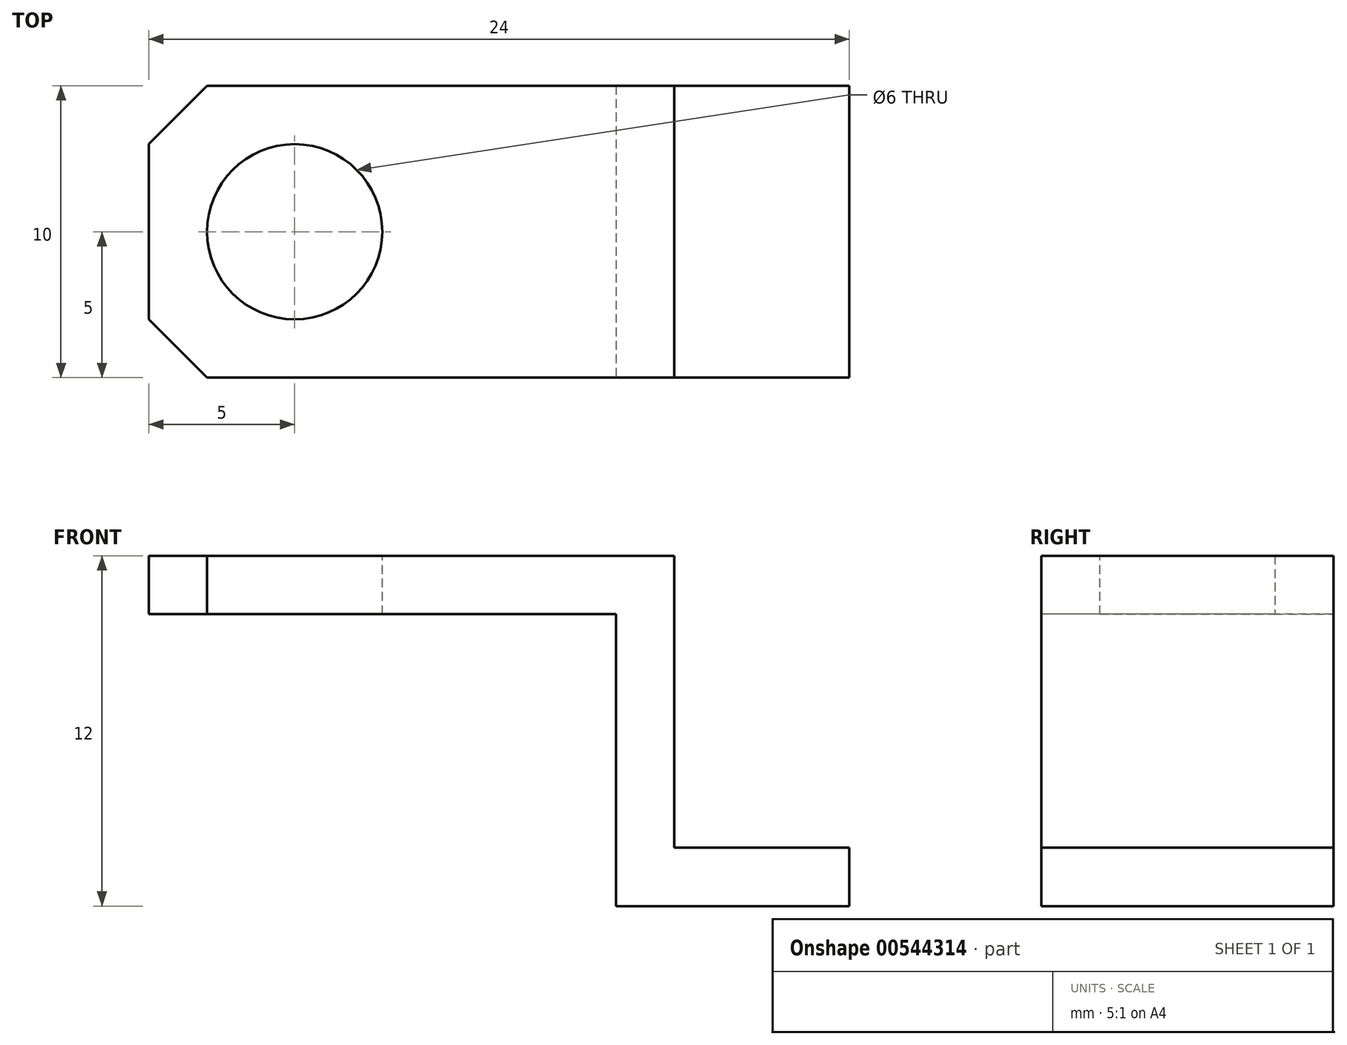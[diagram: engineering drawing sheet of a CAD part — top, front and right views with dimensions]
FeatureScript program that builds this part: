
annotation { "Feature Type Name" : "Feature", "Feature Type Description" : "" }
export const myFeature = defineFeature(function(context is Context, id is Id, definition is map)
    precondition{}
    {
        {
            var Q0;
            Q0=qCreatedBy(makeId("Top.planeOp"),FACE);
            var sketch = newSketch(context, id + "F0", { "sketchPlane" : qUnion([Q0])});
            skLineSegment(sketch, "E0.bottom", {"start": v(0, 0) * mm, "end": v(16, 0) * mm});
            skLineSegment(sketch, "E0.top", {"start": v(0, -10) * mm, "end": v(16, -10) * mm});
            skLineSegment(sketch, "E0.left", {"start": v(0, 0) * mm, "end": v(0, -10) * mm});
            skLineSegment(sketch, "E0.right", {"start": v(16, 0) * mm, "end": v(16, -10) * mm});
            skSolve(sketch);
        }
        {
            var Q0;
            Q0=makeQuery(id+"F0.imprint","IMPRINT",FACE,{"disambiguationData":[TD([[makeQuery(id+"F0.imprint","IMPRINT",EDGE,{"derivedFrom":sQuery(id+"F0.wireOp",EDGE,"E0.bottom")}),-1.0]])]});
            extrude(context, id + "F1", {"entities" : qUnion([Q0]), "depth" : 2 * mm, "offsetDistance" : 25 * mm});
        }
        {
            var Q0;
            Q0=makeQuery(id+"F1.opExtrude","SWEPT_EDGE",EDGE,{"disambiguationData":[OSD([sQuery(id+"F0.wireOp",EDGE,"E0.top"),sQuery(id+"F0.wireOp",EDGE,"E0.left")])]});
            var Q1;
            Q1=makeQuery(id+"F1.opExtrude","SWEPT_EDGE",EDGE,{"disambiguationData":[OSD([sQuery(id+"F0.wireOp",EDGE,"E0.bottom"),sQuery(id+"F0.wireOp",EDGE,"E0.left")])]});
            chamfer(context, id + "F2", {"entities" : qUnion([Q0, Q1]), "width" : 2 * mm, "tangentPropagation" : true});
        }
        {
            var Q0;
            Q0=makeQuery(id+"F1.opExtrude","CAP_FACE",FACE,{"disambiguationData":[OSD([sQuery(id+"F0.wireOp",EDGE,"E0.bottom"),sQuery(id+"F0.wireOp",EDGE,"E0.top"),sQuery(id+"F0.wireOp",EDGE,"E0.left"),sQuery(id+"F0.wireOp",EDGE,"E0.right")])],"isStart":false});
            var sketch = newSketch(context, id + "F3", { "sketchPlane" : qUnion([Q0])});
            skSolve(sketch);
        }
        {
            var Q0;
            Q0=makeQuery(id+"Frxf8R7rs65p3Xx_1.opExtrude","CAP_FACE",FACE,{"disambiguationData":[OSD([sQuery(id+"FzLePIPO3pfEcYt_1.wireOp",EDGE,"ZCLb7Xh7-SzIb-zIYx-FE9R-5UMmaX8gGtaP.bottom"),sQuery(id+"FzLePIPO3pfEcYt_1.wireOp",EDGE,"ZCLb7Xh7-SzIb-zIYx-FE9R-5UMmaX8gGtaP.top"),sQuery(id+"FzLePIPO3pfEcYt_1.wireOp",EDGE,"ZCLb7Xh7-SzIb-zIYx-FE9R-5UMmaX8gGtaP.left"),sQuery(id+"FzLePIPO3pfEcYt_1.wireOp",EDGE,"ZCLb7Xh7-SzIb-zIYx-FE9R-5UMmaX8gGtaP.right")])],"isStart":false});
            var sketch = newSketch(context, id + "F4", { "sketchPlane" : qUnion([Q0])});
            skLineSegment(sketch, "E1.bottom", {"start": v(-10, -11) * mm, "end": v(0, -11) * mm});
            skLineSegment(sketch, "E1.top", {"start": v(-10, -9) * mm, "end": v(0, -9) * mm});
            skLineSegment(sketch, "E1.left", {"start": v(-10, -11) * mm, "end": v(-10, -9) * mm});
            skLineSegment(sketch, "E1.right", {"start": v(0, -11) * mm, "end": v(0, -9) * mm});
            skSolve(sketch);
        }
        {
            var Q0;
            {var subQ0=sQuery(id+"F0.wireOp",EDGE,"E0.right");Q0=makeQuery(id+"F3.imprint","IMPRINT",FACE,{"disambiguationData":[TD([[makeQuery(id+"F3.imprint","IMPRINT",EDGE,{"derivedFrom":makeQuery(id+"F1.opExtrude","CAP_EDGE",EDGE,{"disambiguationData":[OSD([subQ0])],"isStart":false})}),-1.0]])]});}
            var sketch = newSketch(context, id + "F5", { "sketchPlane" : qUnion([Q0])});
            skSolve(sketch);
        }
        {
            var Q0;
            {var subQ1=sQuery(id+"F0.wireOp",EDGE,"E0.right");Q0=makeQuery(id+"F5.imprint","IMPRINT",FACE,{"disambiguationData":[TD([[makeQuery(id+"F5.imprint","IMPRINT",EDGE,{"derivedFrom":makeQuery(id+"F3.imprint","IMPRINT",EDGE,{"derivedFrom":makeQuery(id+"F1.opExtrude","CAP_EDGE",EDGE,{"disambiguationData":[OSD([subQ1])],"isStart":false})})}),-1.0]])]});}
            var sketch = newSketch(context, id + "F6", { "sketchPlane" : qUnion([Q0])});
            skCircle(sketch, "E2", {"center": v(5, -5) * mm, "radius": 3 * mm});
            skSolve(sketch);
        }
        {
            var Q0;
            Q0=sQuery(id+"F6.wireOp",VERTEX,"E2.center");
            var Q1;
            Q1=makeQuery(id+"F1.opExtrude","SWEPT_BODY",BODY,{"disambiguationData":[OSD([sQuery(id+"F0.wireOp",EDGE,"E0.bottom"),sQuery(id+"F0.wireOp",EDGE,"E0.top"),sQuery(id+"F0.wireOp",EDGE,"E0.left"),sQuery(id+"F0.wireOp",EDGE,"E0.right")])]});
            hole(context, id + "F7", {"style" : HoleStyle.SIMPLE, "endStyle" : HoleEndStyle.THROUGH, "holeDiameter" : 6 * mm, "isTappedThrough" : true, "tappedDepth" : 12 * mm, "tapClearance" : 3, "locations" : qUnion([Q0]), "scope" : qUnion([Q1])});
        }
        {
            var Q0;
            Q0=makeQuery(id+"F1.opExtrude","SWEPT_FACE",FACE,{"disambiguationData":[OSD([sQuery(id+"F0.wireOp",EDGE,"E0.right")])]});
            var sketch = newSketch(context, id + "F8", { "sketchPlane" : qUnion([Q0])});
            skLineSegment(sketch, "E3.bottom", {"start": v(-10, 2) * mm, "end": v(0, 2) * mm});
            skLineSegment(sketch, "E3.top", {"start": v(-10, -10) * mm, "end": v(0, -10) * mm});
            skLineSegment(sketch, "E3.left", {"start": v(-10, 2) * mm, "end": v(-10, -10) * mm});
            skLineSegment(sketch, "E3.right", {"start": v(0, 2) * mm, "end": v(0, -10) * mm});
            skSolve(sketch);
        }
        {
            var Q0;
            {var subQ0=sQuery(id+"F8.wireOp",EDGE,"E3.bottom");Q0=makeQuery(id+"F8.imprint","IMPRINT",FACE,{"disambiguationData":[TD([[makeQuery(id+"F8.imprint","IMPRINT",EDGE,{"derivedFrom":subQ0}),1.0]])]});}
            var Q1;
            {var subQ0=sQuery(id+"F8.wireOp",EDGE,"E3.top");Q1=makeQuery(id+"F8.imprint","IMPRINT",FACE,{"disambiguationData":[TD([[makeQuery(id+"F8.imprint","IMPRINT",EDGE,{"derivedFrom":subQ0}),1.0]])]});}
            extrude(context, id + "F9", {"entities" : qUnion([Q0, Q1]), "operationType" : NewBodyOperationType.ADD, "depth" : 2 * mm, "offsetDistance" : 25 * mm});
        }
        {
            var Q0;
            Q0=makeQuery(id+"F9.opExtrude","CAP_FACE",FACE,{"disambiguationData":[OSD([sQuery(id+"F8.wireOp",EDGE,"E3.bottom"),sQuery(id+"F8.wireOp",EDGE,"E3.top"),sQuery(id+"F8.wireOp",EDGE,"E3.left"),sQuery(id+"F8.wireOp",EDGE,"E3.right")])],"isStart":false});
            var sketch = newSketch(context, id + "F10", { "sketchPlane" : qUnion([Q0])});
            skLineSegment(sketch, "E4.bottom", {"start": v(-10, -10) * mm, "end": v(0, -10) * mm});
            skLineSegment(sketch, "E4.top", {"start": v(-10, -8) * mm, "end": v(0, -8) * mm});
            skLineSegment(sketch, "E4.left", {"start": v(-10, -10) * mm, "end": v(-10, -8) * mm});
            skLineSegment(sketch, "E4.right", {"start": v(0, -10) * mm, "end": v(0, -8) * mm});
            skSolve(sketch);
        }
        {
            var Q0;
            Q0=makeQuery(id+"F10.imprint","IMPRINT",FACE,{"disambiguationData":[TD([[makeQuery(id+"F10.imprint","IMPRINT",EDGE,{"derivedFrom":sQuery(id+"F10.wireOp",EDGE,"E4.bottom")}),1.0]])]});
            extrude(context, id + "F11", {"entities" : qUnion([Q0]), "operationType" : NewBodyOperationType.ADD, "depth" : 6 * mm, "offsetDistance" : 25 * mm});
        }
    });
